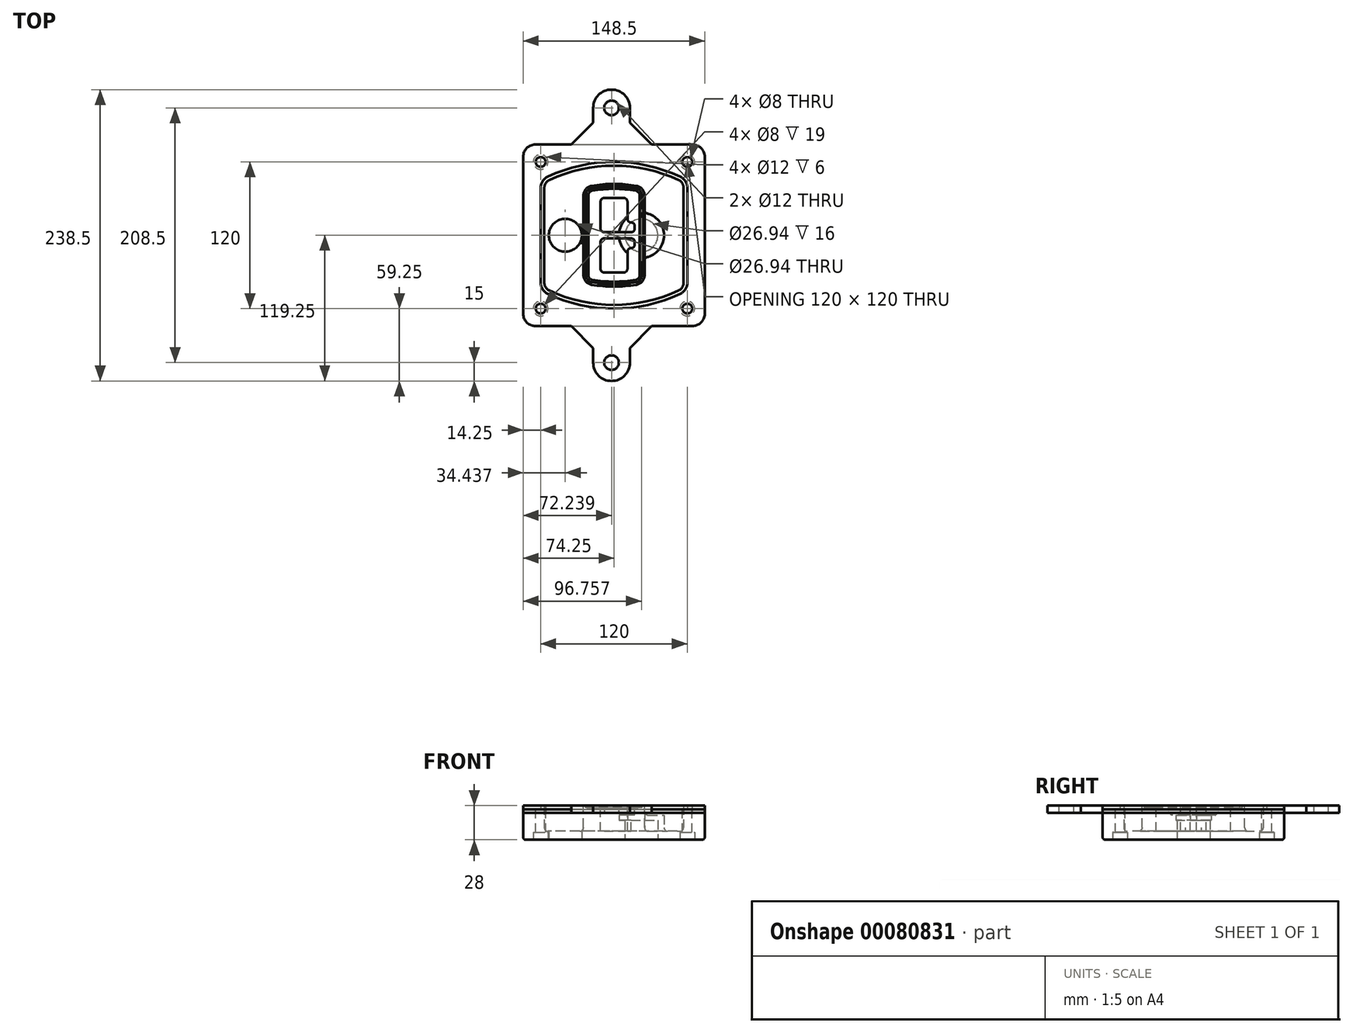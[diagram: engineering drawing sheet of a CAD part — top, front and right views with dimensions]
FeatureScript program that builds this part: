
annotation { "Feature Type Name" : "Feature", "Feature Type Description" : "" }
export const myFeature = defineFeature(function(context is Context, id is Id, definition is map)
    precondition{}
    {
        {
            var Q0;
            Q0=qCreatedBy(makeId("Top.planeOp"),FACE);
            var sketch = newSketch(context, id + "F0", { "sketchPlane" : qUnion([Q0])});
            skPoint(sketch, "E0.rect.middle", {"position": v(0, 0) * mm});
            skLineSegment(sketch, "E1.bottom", {"start": v(-64.25, -74.25) * mm, "end": v(64.25, -74.25) * mm});
            skLineSegment(sketch, "E1.top", {"start": v(-64.25, 74.25) * mm, "end": v(64.25, 74.25) * mm});
            skLineSegment(sketch, "E1.left", {"start": v(-74.25, -64.25) * mm, "end": v(-74.25, 64.25) * mm});
            skLineSegment(sketch, "E1.right", {"start": v(74.25, -64.25) * mm, "end": v(74.25, 64.25) * mm});
            skLineSegment(sketch, "E2", {"start": v(-74.25, 74.25) * mm, "end": v(74.25, -74.25) * mm, "construction": true});
            skLineSegment(sketch, "E3", {"start": v(74.25, 74.25) * mm, "end": v(-74.25, -74.25) * mm, "construction": true});
            skCircle(sketch, "E4", {"center": v(-60, 60) * mm, "radius": 4 * mm});
            skCircle(sketch, "E5", {"center": v(60, 60) * mm, "radius": 4 * mm});
            skCircle(sketch, "E6", {"center": v(60, -60) * mm, "radius": 4 * mm});
            skCircle(sketch, "E7", {"center": v(-60, -60) * mm, "radius": 4 * mm});
            skLineSegment(sketch, "E8", {"start": v(-60, 60) * mm, "end": v(60, 60) * mm, "construction": true});
            skLineSegment(sketch, "E9", {"start": v(60, 60) * mm, "end": v(60, -60) * mm, "construction": true});
            skLineSegment(sketch, "E10", {"start": v(60, -60) * mm, "end": v(-60, -60) * mm, "construction": true});
            skLineSegment(sketch, "E11", {"start": v(-60, -60) * mm, "end": v(-60, 60) * mm, "construction": true});
            skLineSegment(sketch, "E12", {"start": v(-60, 38.83) * mm, "end": v(-60, -38.83) * mm});
            skLineSegment(sketch, "E13", {"start": v(60, 38.83) * mm, "end": v(60, -38.83) * mm});
            skArc(sketch, "E14", {"start": v(54.26, 47.88) * mm, "mid": v(0, 60) * mm, "end": v(-54.26, 47.88) * mm});
            skArc(sketch, "E15", {"start": v(-54.26, -47.88) * mm, "mid": v(0, -60) * mm, "end": v(54.26, -47.88) * mm});
            skLineSegment(sketch, "E16", {"start": v(-60, 0) * mm, "end": v(60, 0) * mm, "construction": true});
            skPoint(sketch, "E17.visualSharp", {"position": v(-60, -45) * mm});
            skArc(sketch, "E17.filletArc", {"start": v(-60, -38.83) * mm, "mid": v(-58.44, -44.2) * mm, "end": v(-54.26, -47.88) * mm});
            skPoint(sketch, "E18.visualSharp", {"position": v(-60, 45) * mm});
            skArc(sketch, "E18.filletArc", {"start": v(-54.26, 47.88) * mm, "mid": v(-58.44, 44.2) * mm, "end": v(-60, 38.83) * mm});
            skPoint(sketch, "E19.visualSharp", {"position": v(60, 45) * mm});
            skArc(sketch, "E19.filletArc", {"start": v(60, 38.83) * mm, "mid": v(58.44, 44.2) * mm, "end": v(54.26, 47.88) * mm});
            skPoint(sketch, "E20.visualSharp", {"position": v(60, -45) * mm});
            skArc(sketch, "E20.filletArc", {"start": v(54.26, -47.88) * mm, "mid": v(58.44, -44.2) * mm, "end": v(60, -38.83) * mm});
            skPoint(sketch, "E21.visualSharp", {"position": v(-74.25, 74.25) * mm});
            skArc(sketch, "E21.filletArc", {"start": v(-64.25, 74.25) * mm, "mid": v(-71.32, 71.32) * mm, "end": v(-74.25, 64.25) * mm});
            skPoint(sketch, "E22.visualSharp", {"position": v(74.25, 74.25) * mm});
            skArc(sketch, "E22.filletArc", {"start": v(74.25, 64.25) * mm, "mid": v(71.32, 71.32) * mm, "end": v(64.25, 74.25) * mm});
            skPoint(sketch, "E23.visualSharp", {"position": v(74.25, -74.25) * mm});
            skArc(sketch, "E23.filletArc", {"start": v(64.25, -74.25) * mm, "mid": v(71.32, -71.32) * mm, "end": v(74.25, -64.25) * mm});
            skPoint(sketch, "E24.visualSharp", {"position": v(-74.25, -74.25) * mm});
            skArc(sketch, "E24.filletArc", {"start": v(-74.25, -64.25) * mm, "mid": v(-71.32, -71.32) * mm, "end": v(-64.25, -74.25) * mm});
            skArc(sketch, "E25.0", {"start": v(57, 38.83) * mm, "mid": v(55.9, 42.58) * mm, "end": v(52.98, 45.17) * mm});
            skLineSegment(sketch, "E25.1", {"start": v(57, 38.83) * mm, "end": v(57, -38.83) * mm});
            skArc(sketch, "E25.2", {"start": v(52.98, -45.17) * mm, "mid": v(55.9, -42.58) * mm, "end": v(57, -38.83) * mm});
            skArc(sketch, "E25.3", {"start": v(-52.98, -45.17) * mm, "mid": v(0, -57) * mm, "end": v(52.98, -45.17) * mm});
            skArc(sketch, "E25.4", {"start": v(-57, -38.83) * mm, "mid": v(-55.9, -42.58) * mm, "end": v(-52.98, -45.17) * mm});
            skArc(sketch, "E25.5", {"start": v(52.98, 45.17) * mm, "mid": v(0, 57) * mm, "end": v(-52.98, 45.17) * mm});
            skLineSegment(sketch, "E25.6", {"start": v(-57, 38.83) * mm, "end": v(-57, -38.83) * mm});
            skArc(sketch, "E25.7", {"start": v(-52.98, 45.17) * mm, "mid": v(-55.9, 42.58) * mm, "end": v(-57, 38.83) * mm});
            skArc(sketch, "E26.0", {"start": v(-55.96, 51.5) * mm, "mid": v(-61.82, 46.33) * mm, "end": v(-64, 38.83) * mm});
            skArc(sketch, "E26.1", {"start": v(55.96, 51.5) * mm, "mid": v(0, 64) * mm, "end": v(-55.96, 51.5) * mm});
            skArc(sketch, "E26.2", {"start": v(64, 38.83) * mm, "mid": v(61.82, 46.33) * mm, "end": v(55.96, 51.5) * mm});
            skLineSegment(sketch, "E26.3", {"start": v(64, 38.83) * mm, "end": v(64, -38.83) * mm});
            skArc(sketch, "E26.4", {"start": v(55.96, -51.5) * mm, "mid": v(61.82, -46.33) * mm, "end": v(64, -38.83) * mm});
            skLineSegment(sketch, "E26.5", {"start": v(-64, 38.83) * mm, "end": v(-64, -38.83) * mm});
            skArc(sketch, "E26.6", {"start": v(-55.96, -51.5) * mm, "mid": v(0, -64) * mm, "end": v(55.96, -51.5) * mm});
            skArc(sketch, "E26.7", {"start": v(-64, -38.83) * mm, "mid": v(-61.82, -46.33) * mm, "end": v(-55.96, -51.5) * mm});
            skSolve(sketch);
        }
        {
            var Q0;
            Q0=makeQuery(id+"F0.imprint","IMPRINT",FACE,{"disambiguationData":[TD([[makeQuery(id+"F0.imprint","IMPRINT",EDGE,{"derivedFrom":sQuery(id+"F0.wireOp",EDGE,"E1.bottom")}),1.0]])]});
            var Q1;
            Q1=makeQuery(id+"F0.imprint","IMPRINT",FACE,{"disambiguationData":[TD([[makeQuery(id+"F0.imprint","IMPRINT",EDGE,{"derivedFrom":sQuery(id+"F0.wireOp",EDGE,"E12")}),1.0]])]});
            var Q2;
            Q2=makeQuery(id+"F0.imprint","IMPRINT",FACE,{"disambiguationData":[TD([[makeQuery(id+"F0.imprint","IMPRINT",EDGE,{"derivedFrom":sQuery(id+"F0.wireOp",EDGE,"E25.0")}),1.0]])]});
            var Q3;
            Q3=makeQuery(id+"F0.imprint","IMPRINT",FACE,{"disambiguationData":[TD([[makeQuery(id+"F0.imprint","IMPRINT",EDGE,{"derivedFrom":sQuery(id+"F0.wireOp",EDGE,"E12")}),-1.0]])]});
            extrude(context, id + "F1", {"entities" : qUnion([Q0, Q1, Q2, Q3]), "oppositeDirection" : true, "depth" : 25 * mm});
        }
        {
            var Q0;
            Q0=makeQuery(id+"F0.imprint","IMPRINT",FACE,{"disambiguationData":[TD([[makeQuery(id+"F0.imprint","IMPRINT",EDGE,{"derivedFrom":sQuery(id+"F0.wireOp",EDGE,"E12")}),1.0]])]});
            extrude(context, id + "F2", {"entities" : qUnion([Q0]), "operationType" : NewBodyOperationType.ADD, "depth" : 3 * mm});
        }
        {
            var Q0;
            Q0=makeQuery(id+"F0.imprint","IMPRINT",FACE,{"disambiguationData":[TD([[makeQuery(id+"F0.imprint","IMPRINT",EDGE,{"derivedFrom":sQuery(id+"F0.wireOp",EDGE,"E25.0")}),1.0]])]});
            extrude(context, id + "F3", {"entities" : qUnion([Q0]), "operationType" : NewBodyOperationType.REMOVE, "oppositeDirection" : true, "depth" : 18 * mm});
        }
        {
            var Q0;
            Q0=makeQuery(id+"F2.opExtrude","CAP_FACE",FACE,{"disambiguationData":[OSD([sQuery(id+"F0.wireOp",EDGE,"E12"),sQuery(id+"F0.wireOp",EDGE,"E13"),sQuery(id+"F0.wireOp",EDGE,"E14"),sQuery(id+"F0.wireOp",EDGE,"E15"),sQuery(id+"F0.wireOp",EDGE,"E17.filletArc"),sQuery(id+"F0.wireOp",EDGE,"E18.filletArc"),sQuery(id+"F0.wireOp",EDGE,"E19.filletArc"),sQuery(id+"F0.wireOp",EDGE,"E20.filletArc"),sQuery(id+"F0.wireOp",EDGE,"E25.0"),sQuery(id+"F0.wireOp",EDGE,"E25.1"),sQuery(id+"F0.wireOp",EDGE,"E25.2"),sQuery(id+"F0.wireOp",EDGE,"E25.3"),sQuery(id+"F0.wireOp",EDGE,"E25.4"),sQuery(id+"F0.wireOp",EDGE,"E25.5"),sQuery(id+"F0.wireOp",EDGE,"E25.6"),sQuery(id+"F0.wireOp",EDGE,"E25.7")])],"isStart":false});
            var sketch = newSketch(context, id + "F4", { "sketchPlane" : qUnion([Q0])});
            skArc(sketch, "E27.0", {"start": v(-18.34, -40.45) * mm, "mid": v(0, -42) * mm, "end": v(18.34, -40.45) * mm});
            skArc(sketch, "E28.0", {"start": v(18.34, 40.45) * mm, "mid": v(0, 42) * mm, "end": v(-18.34, 40.45) * mm});
            skLineSegment(sketch, "E29", {"start": v(-25, 32.57) * mm, "end": v(-25, -32.57) * mm});
            skLineSegment(sketch, "E30", {"start": v(25, 32.57) * mm, "end": v(25, -32.57) * mm});
            skLineSegment(sketch, "E31", {"start": v(-25, 39.1) * mm, "end": v(25, 39.1) * mm, "construction": true});
            skLineSegment(sketch, "E32", {"start": v(-25, -39.1) * mm, "end": v(25, -39.1) * mm, "construction": true});
            skPoint(sketch, "E33.visualSharp", {"position": v(-25, 39.1) * mm});
            skArc(sketch, "E33.filletArc", {"start": v(-18.34, 40.45) * mm, "mid": v(-23.11, 37.73) * mm, "end": v(-25, 32.57) * mm});
            skPoint(sketch, "E34.visualSharp", {"position": v(25, 39.1) * mm});
            skArc(sketch, "E34.filletArc", {"start": v(25, 32.57) * mm, "mid": v(23.11, 37.73) * mm, "end": v(18.34, 40.45) * mm});
            skPoint(sketch, "E35.visualSharp", {"position": v(25, -39.1) * mm});
            skArc(sketch, "E35.filletArc", {"start": v(18.34, -40.45) * mm, "mid": v(23.11, -37.73) * mm, "end": v(25, -32.57) * mm});
            skPoint(sketch, "E36.visualSharp", {"position": v(-25, -39.1) * mm});
            skArc(sketch, "E36.filletArc", {"start": v(-25, -32.57) * mm, "mid": v(-23.11, -37.73) * mm, "end": v(-18.34, -40.45) * mm});
            skArc(sketch, "E37.0", {"start": v(52.98, 45.17) * mm, "mid": v(0, 57) * mm, "end": v(-52.98, 45.17) * mm});
            skArc(sketch, "E37.1", {"start": v(-52.98, 45.17) * mm, "mid": v(-55.9, 42.58) * mm, "end": v(-57, 38.83) * mm});
            skLineSegment(sketch, "E37.2", {"start": v(-57, 38.83) * mm, "end": v(-57, -38.83) * mm});
            skArc(sketch, "E37.3", {"start": v(-57, -38.83) * mm, "mid": v(-55.9, -42.58) * mm, "end": v(-52.98, -45.17) * mm});
            skArc(sketch, "E37.4", {"start": v(-52.98, -45.17) * mm, "mid": v(0, -57) * mm, "end": v(52.98, -45.17) * mm});
            skArc(sketch, "E37.5", {"start": v(52.98, -45.17) * mm, "mid": v(55.9, -42.58) * mm, "end": v(57, -38.83) * mm});
            skLineSegment(sketch, "E37.6", {"start": v(57, 38.83) * mm, "end": v(57, -38.83) * mm});
            skArc(sketch, "E37.7", {"start": v(57, 38.83) * mm, "mid": v(55.9, 42.58) * mm, "end": v(52.98, 45.17) * mm});
            skLineSegment(sketch, "E38.0", {"start": v(23, 32.57) * mm, "end": v(23, -32.57) * mm});
            skArc(sketch, "E38.1", {"start": v(18, -38.48) * mm, "mid": v(21.58, -36.44) * mm, "end": v(23, -32.57) * mm});
            skArc(sketch, "E38.2", {"start": v(-18, -38.48) * mm, "mid": v(0, -40) * mm, "end": v(18, -38.48) * mm});
            skArc(sketch, "E38.3", {"start": v(-23, -32.57) * mm, "mid": v(-21.58, -36.44) * mm, "end": v(-18, -38.48) * mm});
            skLineSegment(sketch, "E38.4", {"start": v(-23, 32.57) * mm, "end": v(-23, -32.57) * mm});
            skArc(sketch, "E38.5", {"start": v(23, 32.57) * mm, "mid": v(21.58, 36.44) * mm, "end": v(18, 38.48) * mm});
            skArc(sketch, "E38.6", {"start": v(-18, 38.48) * mm, "mid": v(-21.58, 36.44) * mm, "end": v(-23, 32.57) * mm});
            skArc(sketch, "E38.7", {"start": v(18, 38.48) * mm, "mid": v(0, 40) * mm, "end": v(-18, 38.48) * mm});
            skArc(sketch, "E39.0", {"start": v(21, 32.57) * mm, "mid": v(20.06, 35.15) * mm, "end": v(17.67, 36.5) * mm});
            skLineSegment(sketch, "E39.1", {"start": v(21, 32.57) * mm, "end": v(21, -32.57) * mm});
            skArc(sketch, "E39.2", {"start": v(17.67, -36.5) * mm, "mid": v(20.06, -35.15) * mm, "end": v(21, -32.57) * mm});
            skArc(sketch, "E39.3", {"start": v(-17.67, -36.5) * mm, "mid": v(0, -38) * mm, "end": v(17.67, -36.5) * mm});
            skArc(sketch, "E39.4", {"start": v(-21, -32.57) * mm, "mid": v(-20.06, -35.15) * mm, "end": v(-17.67, -36.5) * mm});
            skArc(sketch, "E39.5", {"start": v(17.67, 36.5) * mm, "mid": v(0, 38) * mm, "end": v(-17.67, 36.5) * mm});
            skLineSegment(sketch, "E39.6", {"start": v(-21, 32.57) * mm, "end": v(-21, -32.57) * mm});
            skArc(sketch, "E39.7", {"start": v(-17.67, 36.5) * mm, "mid": v(-20.06, 35.15) * mm, "end": v(-21, 32.57) * mm});
            skLineSegment(sketch, "E40", {"start": v(-25, 0) * mm, "end": v(25, 0) * mm, "construction": true});
            skLineSegment(sketch, "E41", {"start": v(-11, 5.5) * mm, "end": v(-11, 27.5) * mm});
            skLineSegment(sketch, "E42", {"start": v(-8, 30.5) * mm, "end": v(8, 30.5) * mm});
            skLineSegment(sketch, "E43", {"start": v(11, 27.5) * mm, "end": v(11, 13.5) * mm});
            skLineSegment(sketch, "E44", {"start": v(14, 10.5) * mm, "end": v(14, 10.5) * mm});
            skLineSegment(sketch, "E45", {"start": v(17, 7.5) * mm, "end": v(17, 5.5) * mm});
            skLineSegment(sketch, "E46", {"start": v(14, 2.5) * mm, "end": v(-8, 2.5) * mm});
            skPoint(sketch, "E47.visualSharp", {"position": v(-11, 30.5) * mm});
            skArc(sketch, "E47.filletArc", {"start": v(-8, 30.5) * mm, "mid": v(-10.12, 29.62) * mm, "end": v(-11, 27.5) * mm});
            skPoint(sketch, "E48.visualSharp", {"position": v(11, 30.5) * mm});
            skArc(sketch, "E48.filletArc", {"start": v(11, 27.5) * mm, "mid": v(10.12, 29.62) * mm, "end": v(8, 30.5) * mm});
            skPoint(sketch, "E49.visualSharp", {"position": v(11, 10.5) * mm});
            skArc(sketch, "E49.filletArc", {"start": v(11, 13.5) * mm, "mid": v(11.88, 11.38) * mm, "end": v(14, 10.5) * mm});
            skPoint(sketch, "E50.visualSharp", {"position": v(17, 10.5) * mm});
            skArc(sketch, "E50.filletArc", {"start": v(17, 7.5) * mm, "mid": v(16.12, 9.62) * mm, "end": v(14, 10.5) * mm});
            skPoint(sketch, "E51.visualSharp", {"position": v(17, 2.5) * mm});
            skArc(sketch, "E51.filletArc", {"start": v(14, 2.5) * mm, "mid": v(16.12, 3.38) * mm, "end": v(17, 5.5) * mm});
            skPoint(sketch, "E52.visualSharp", {"position": v(-11, 2.5) * mm});
            skArc(sketch, "E52.filletArc", {"start": v(-11, 5.5) * mm, "mid": v(-10.12, 3.38) * mm, "end": v(-8, 2.5) * mm});
            skLineSegment(sketch, "E53.0.MirrorCS", {"start": v(14, -2.5) * mm, "end": v(-8, -2.5) * mm});
            skArc(sketch, "E54.0.MirrorCS", {"start": v(-11, -5.5) * mm, "mid": v(-10.12, -3.38) * mm, "end": v(-8, -2.5) * mm});
            skLineSegment(sketch, "E55.0.MirrorCS", {"start": v(-11, -5.5) * mm, "end": v(-11, -27.5) * mm});
            skArc(sketch, "E56.0.MirrorCS", {"start": v(-8, -30.5) * mm, "mid": v(-10.12, -29.62) * mm, "end": v(-11, -27.5) * mm});
            skLineSegment(sketch, "E57.0.MirrorCS", {"start": v(-8, -30.5) * mm, "end": v(8, -30.5) * mm});
            skArc(sketch, "E58.0.MirrorCS", {"start": v(11, -27.5) * mm, "mid": v(10.12, -29.62) * mm, "end": v(8, -30.5) * mm});
            skLineSegment(sketch, "E59.0.MirrorCS", {"start": v(11, -27.5) * mm, "end": v(11, -13.5) * mm});
            skArc(sketch, "E60.0.MirrorCS", {"start": v(11, -13.5) * mm, "mid": v(11.88, -11.38) * mm, "end": v(14, -10.5) * mm});
            skArc(sketch, "E61.0.MirrorCS", {"start": v(17, -7.5) * mm, "mid": v(16.12, -9.62) * mm, "end": v(14, -10.5) * mm});
            skLineSegment(sketch, "E62.0.MirrorCS", {"start": v(17, -7.5) * mm, "end": v(17, -5.5) * mm});
            skArc(sketch, "E63.0.MirrorCS", {"start": v(14, -2.5) * mm, "mid": v(16.12, -3.38) * mm, "end": v(17, -5.5) * mm});
            skSolve(sketch);
        }
        {
            var Q0;
            Q0=makeQuery(id+"F4.imprint","IMPRINT",FACE,{"disambiguationData":[TD([[makeQuery(id+"F4.imprint","IMPRINT",EDGE,{"derivedFrom":sQuery(id+"F4.wireOp",EDGE,"E27.0")}),1.0]])]});
            var Q1;
            Q1=makeQuery(id+"F4.imprint","IMPRINT",FACE,{"disambiguationData":[TD([[makeQuery(id+"F4.imprint","IMPRINT",EDGE,{"derivedFrom":sQuery(id+"F4.wireOp",EDGE,"E38.0")}),-1.0]])]});
            var Q2;
            Q2=makeQuery(id+"F4.imprint","IMPRINT",FACE,{"disambiguationData":[TD([[makeQuery(id+"F4.imprint","IMPRINT",EDGE,{"derivedFrom":sQuery(id+"F4.wireOp",EDGE,"E39.0")}),1.0]])]});
            extrude(context, id + "F5", {"entities" : qUnion([Q0, Q1, Q2]), "operationType" : NewBodyOperationType.ADD, "endBound" : BoundingType.UP_TO_NEXT, "oppositeDirection" : true, "depth" : 25 * mm});
        }
        {
            var Q0;
            Q0=makeQuery(id+"F4.imprint","IMPRINT",FACE,{"disambiguationData":[TD([[makeQuery(id+"F4.imprint","IMPRINT",EDGE,{"derivedFrom":sQuery(id+"F4.wireOp",EDGE,"E38.0")}),-1.0]])]});
            extrude(context, id + "F6", {"entities" : qUnion([Q0]), "operationType" : NewBodyOperationType.REMOVE, "oppositeDirection" : true, "depth" : 2 * mm});
        }
        {
            var Q0;
            Q0=makeQuery(id+"F1.opExtrude","CAP_FACE",FACE,{"disambiguationData":[OSD([sQuery(id+"F0.wireOp",EDGE,"E1.bottom"),sQuery(id+"F0.wireOp",EDGE,"E1.top"),sQuery(id+"F0.wireOp",EDGE,"E1.left"),sQuery(id+"F0.wireOp",EDGE,"E1.right"),sQuery(id+"F0.wireOp",EDGE,"E4"),sQuery(id+"F0.wireOp",EDGE,"E5"),sQuery(id+"F0.wireOp",EDGE,"E6"),sQuery(id+"F0.wireOp",EDGE,"E7"),sQuery(id+"F0.wireOp",EDGE,"E21.filletArc"),sQuery(id+"F0.wireOp",EDGE,"E22.filletArc"),sQuery(id+"F0.wireOp",EDGE,"E23.filletArc"),sQuery(id+"F0.wireOp",EDGE,"E24.filletArc")])],"isStart":false});
            var sketch = newSketch(context, id + "F7", { "sketchPlane" : qUnion([Q0])});
            skCircle(sketch, "E64", {"center": v(22.5, 0) * mm, "radius": 13.47 * mm});
            skCircle(sketch, "E65", {"center": v(-39.81, 0) * mm, "radius": 13.47 * mm});
            skLineSegment(sketch, "E66", {"start": v(74.25, 0) * mm, "end": v(-74.25, 0) * mm});
            skCircle(sketch, "E67", {"center": v(22.5, 0) * mm, "radius": 18.47 * mm});
            skCircle(sketch, "E68", {"center": v(60, -60) * mm, "radius": 6 * mm});
            skCircle(sketch, "E69", {"center": v(-60, -60) * mm, "radius": 6 * mm});
            skCircle(sketch, "E70", {"center": v(-60, 60) * mm, "radius": 6 * mm});
            skCircle(sketch, "E71", {"center": v(60, 60) * mm, "radius": 6 * mm});
            skSolve(sketch);
        }
        {
            var Q0;
            {var subQ1=sQuery(id+"F7.wireOp",EDGE,"E66");var subQ4=sQuery(id+"F7.wireOp",EDGE,"E64");var subQ6=makeQuery(id+"F7.imprint","INTERSECT",VERTEX,{"disambiguationData":[OD(0.0)],"derivedFrom":[subQ4,subQ1]});Q0=makeQuery(id+"F7.imprint","IMPRINT",FACE,{"disambiguationData":[TD([[makeQuery(id+"F7.imprint","IMPRINT",EDGE,{"disambiguationData":[TD([[subQ6,-1.0]])],"derivedFrom":subQ4}),-1.0]])]});}
            var Q1;
            {var subQ0=sQuery(id+"F7.wireOp",EDGE,"E66");var subQ1=sQuery(id+"F7.wireOp",EDGE,"E64");var subQ3=makeQuery(id+"F7.imprint","INTERSECT",VERTEX,{"disambiguationData":[OD(0.0)],"derivedFrom":[subQ1,subQ0]});Q1=makeQuery(id+"F7.imprint","IMPRINT",FACE,{"disambiguationData":[TD([[makeQuery(id+"F7.imprint","IMPRINT",EDGE,{"disambiguationData":[TD([[subQ3,-1.0]])],"derivedFrom":subQ1}),1.0]])]});}
            var Q2;
            {var subQ0=sQuery(id+"F7.wireOp",EDGE,"E66");var subQ1=sQuery(id+"F7.wireOp",EDGE,"E64");var subQ3=makeQuery(id+"F7.imprint","INTERSECT",VERTEX,{"disambiguationData":[OD(0.0)],"derivedFrom":[subQ1,subQ0]});Q2=makeQuery(id+"F7.imprint","IMPRINT",FACE,{"disambiguationData":[TD([[makeQuery(id+"F7.imprint","IMPRINT",EDGE,{"disambiguationData":[TD([[subQ3,1.0]])],"derivedFrom":subQ1}),1.0]])]});}
            var Q3;
            {var subQ1=sQuery(id+"F7.wireOp",EDGE,"E66");var subQ4=sQuery(id+"F7.wireOp",EDGE,"E64");var subQ6=makeQuery(id+"F7.imprint","INTERSECT",VERTEX,{"disambiguationData":[OD(0.0)],"derivedFrom":[subQ4,subQ1]});Q3=makeQuery(id+"F7.imprint","IMPRINT",FACE,{"disambiguationData":[TD([[makeQuery(id+"F7.imprint","IMPRINT",EDGE,{"disambiguationData":[TD([[subQ6,1.0]])],"derivedFrom":subQ4}),-1.0]])]});}
            extrude(context, id + "F8", {"entities" : qUnion([Q0, Q1, Q2, Q3]), "operationType" : NewBodyOperationType.ADD, "oppositeDirection" : true, "depth" : 20 * mm});
        }
        {
            var Q0;
            {var subQ0=sQuery(id+"F7.wireOp",EDGE,"E66");var subQ1=sQuery(id+"F7.wireOp",EDGE,"E64");var subQ3=makeQuery(id+"F7.imprint","INTERSECT",VERTEX,{"disambiguationData":[OD(0.0)],"derivedFrom":[subQ1,subQ0]});Q0=makeQuery(id+"F7.imprint","IMPRINT",FACE,{"disambiguationData":[TD([[makeQuery(id+"F7.imprint","IMPRINT",EDGE,{"disambiguationData":[TD([[subQ3,-1.0]])],"derivedFrom":subQ1}),1.0]])]});}
            var Q1;
            {var subQ0=sQuery(id+"F7.wireOp",EDGE,"E66");var subQ1=sQuery(id+"F7.wireOp",EDGE,"E64");var subQ3=makeQuery(id+"F7.imprint","INTERSECT",VERTEX,{"disambiguationData":[OD(0.0)],"derivedFrom":[subQ1,subQ0]});Q1=makeQuery(id+"F7.imprint","IMPRINT",FACE,{"disambiguationData":[TD([[makeQuery(id+"F7.imprint","IMPRINT",EDGE,{"disambiguationData":[TD([[subQ3,1.0]])],"derivedFrom":subQ1}),1.0]])]});}
            extrude(context, id + "F9", {"entities" : qUnion([Q0, Q1]), "operationType" : NewBodyOperationType.REMOVE, "oppositeDirection" : true, "depth" : 16 * mm});
        }
        {
            var Q0;
            {var subQ0=sQuery(id+"F7.wireOp",EDGE,"E66");var subQ1=sQuery(id+"F7.wireOp",EDGE,"E65");var subQ3=makeQuery(id+"F7.imprint","INTERSECT",VERTEX,{"disambiguationData":[OD(0.0)],"derivedFrom":[subQ1,subQ0]});Q0=makeQuery(id+"F7.imprint","IMPRINT",FACE,{"disambiguationData":[TD([[makeQuery(id+"F7.imprint","IMPRINT",EDGE,{"disambiguationData":[TD([[subQ3,-1.0]])],"derivedFrom":subQ1}),1.0]])]});}
            var Q1;
            {var subQ0=sQuery(id+"F7.wireOp",EDGE,"E66");var subQ1=sQuery(id+"F7.wireOp",EDGE,"E65");var subQ3=makeQuery(id+"F7.imprint","INTERSECT",VERTEX,{"disambiguationData":[OD(0.0)],"derivedFrom":[subQ1,subQ0]});Q1=makeQuery(id+"F7.imprint","IMPRINT",FACE,{"disambiguationData":[TD([[makeQuery(id+"F7.imprint","IMPRINT",EDGE,{"disambiguationData":[TD([[subQ3,1.0]])],"derivedFrom":subQ1}),1.0]])]});}
            extrude(context, id + "F10", {"entities" : qUnion([Q0, Q1]), "operationType" : NewBodyOperationType.REMOVE, "oppositeDirection" : true, "depth" : 25 * mm});
        }
        {
            var Q0;
            Q0=makeQuery(id+"F7.imprint","IMPRINT",FACE,{"disambiguationData":[TD([[makeQuery(id+"F7.imprint","IMPRINT",EDGE,{"derivedFrom":sQuery(id+"F7.wireOp",EDGE,"E68")}),1.0]])]});
            var Q1;
            Q1=makeQuery(id+"F7.imprint","IMPRINT",FACE,{"disambiguationData":[TD([[makeQuery(id+"F7.imprint","IMPRINT",EDGE,{"derivedFrom":makeQuery(id+"F1.opExtrude","CAP_EDGE",EDGE,{"disambiguationData":[OSD([sQuery(id+"F0.wireOp",EDGE,"E5")])],"isStart":false})}),-1.0]])]});
            var Q2;
            Q2=makeQuery(id+"F7.imprint","IMPRINT",FACE,{"disambiguationData":[TD([[makeQuery(id+"F7.imprint","IMPRINT",EDGE,{"derivedFrom":sQuery(id+"F7.wireOp",EDGE,"E69")}),1.0]])]});
            var Q3;
            Q3=makeQuery(id+"F7.imprint","IMPRINT",FACE,{"disambiguationData":[TD([[makeQuery(id+"F7.imprint","IMPRINT",EDGE,{"derivedFrom":makeQuery(id+"F1.opExtrude","CAP_EDGE",EDGE,{"disambiguationData":[OSD([sQuery(id+"F0.wireOp",EDGE,"E4")])],"isStart":false})}),-1.0]])]});
            var Q4;
            Q4=makeQuery(id+"F7.imprint","IMPRINT",FACE,{"disambiguationData":[TD([[makeQuery(id+"F7.imprint","IMPRINT",EDGE,{"derivedFrom":sQuery(id+"F7.wireOp",EDGE,"E70")}),1.0]])]});
            var Q5;
            Q5=makeQuery(id+"F7.imprint","IMPRINT",FACE,{"disambiguationData":[TD([[makeQuery(id+"F7.imprint","IMPRINT",EDGE,{"derivedFrom":makeQuery(id+"F1.opExtrude","CAP_EDGE",EDGE,{"disambiguationData":[OSD([sQuery(id+"F0.wireOp",EDGE,"E7")])],"isStart":false})}),-1.0]])]});
            var Q6;
            Q6=makeQuery(id+"F7.imprint","IMPRINT",FACE,{"disambiguationData":[TD([[makeQuery(id+"F7.imprint","IMPRINT",EDGE,{"derivedFrom":sQuery(id+"F7.wireOp",EDGE,"E71")}),1.0]])]});
            var Q7;
            Q7=makeQuery(id+"F7.imprint","IMPRINT",FACE,{"disambiguationData":[TD([[makeQuery(id+"F7.imprint","IMPRINT",EDGE,{"derivedFrom":makeQuery(id+"F1.opExtrude","CAP_EDGE",EDGE,{"disambiguationData":[OSD([sQuery(id+"F0.wireOp",EDGE,"E6")])],"isStart":false})}),-1.0]])]});
            extrude(context, id + "F11", {"entities" : qUnion([Q0, Q1, Q2, Q3, Q4, Q5, Q6, Q7]), "operationType" : NewBodyOperationType.REMOVE, "oppositeDirection" : true, "depth" : 6 * mm});
        }
        {
            var Q0;
            Q0=makeQuery(id+"F9.boolean.opBoolean","COPY",FACE,{"derivedFrom":makeQuery(id+"F9.opExtrude","CAP_FACE",FACE,{"disambiguationData":[OSD([sQuery(id+"F7.wireOp",EDGE,"E64")])],"isStart":false})});
            var sketch = newSketch(context, id + "F12", { "sketchPlane" : qUnion([Q0])});
            skArc(sketch, "E72.0", {"start": v(11, 14.45) * mm, "mid": v(6.45, 9.13) * mm, "end": v(4.2, 2.5) * mm});
            skArc(sketch, "E72.1", {"start": v(4.2, -2.5) * mm, "mid": v(6.45, -9.13) * mm, "end": v(11, -14.45) * mm});
            skLineSegment(sketch, "E73", {"start": v(4.2, -2.5) * mm, "end": v(14, -2.5) * mm});
            skLineSegment(sketch, "E74.0", {"start": v(14, 2.5) * mm, "end": v(4.2, 2.5) * mm});
            skArc(sketch, "E74.1", {"start": v(14, 2.5) * mm, "mid": v(16.12, 3.38) * mm, "end": v(17, 5.5) * mm});
            skLineSegment(sketch, "E74.2", {"start": v(17, 7.5) * mm, "end": v(17, 5.5) * mm});
            skArc(sketch, "E74.3", {"start": v(17, 7.5) * mm, "mid": v(16.12, 9.62) * mm, "end": v(14, 10.5) * mm});
            skArc(sketch, "E74.4", {"start": v(11, 13.5) * mm, "mid": v(11.88, 11.38) * mm, "end": v(14, 10.5) * mm});
            skLineSegment(sketch, "E74.5", {"start": v(11, 14.45) * mm, "end": v(11, 13.5) * mm});
            skLineSegment(sketch, "E74.7", {"start": v(14, -2.5) * mm, "end": v(4.2, -2.5) * mm});
            skArc(sketch, "E74.8", {"start": v(14, -2.5) * mm, "mid": v(16.12, -3.38) * mm, "end": v(17, -5.5) * mm});
            skLineSegment(sketch, "E74.9", {"start": v(17, -7.5) * mm, "end": v(17, -5.5) * mm});
            skArc(sketch, "E74.10", {"start": v(17, -7.5) * mm, "mid": v(16.12, -9.62) * mm, "end": v(14, -10.5) * mm});
            skArc(sketch, "E74.11", {"start": v(11, -13.5) * mm, "mid": v(11.88, -11.38) * mm, "end": v(14, -10.5) * mm});
            skLineSegment(sketch, "E74.12", {"start": v(11, -14.45) * mm, "end": v(11, -13.5) * mm});
            skPoint(sketch, "E75.orphan", {"position": v(11, -27.5) * mm});
            skPoint(sketch, "E76.orphan", {"position": v(-8, -2.5) * mm});
            skPoint(sketch, "E77.orphan", {"position": v(-8, 2.5) * mm});
            skPoint(sketch, "E78.orphan", {"position": v(11, 27.5) * mm});
            skSolve(sketch);
        }
        {
            var Q0;
            {var subQ7=sQuery(id+"F12.wireOp",EDGE,"E72.0");var subQ14=sQuery(id+"F12.wireOp",EDGE,"E72.1");var subQ16=sQuery(id+"F12.wireOp",EDGE,"E74.1");var subQ18=sQuery(id+"F12.wireOp",EDGE,"E74.8");Q0=qUnion([makeQuery(id+"F12.imprint","IMPRINT",FACE,{"disambiguationData":[TD([[makeQuery(id+"F12.imprint","IMPRINT",EDGE,{"derivedFrom":subQ7}),1.0]])]}),makeQuery(id+"F12.imprint","IMPRINT",FACE,{"disambiguationData":[TD([[makeQuery(id+"F12.imprint","IMPRINT",EDGE,{"derivedFrom":subQ14}),1.0]])]}),makeQuery(id+"F12.imprint","IMPRINT",FACE,{"disambiguationData":[TD([[makeQuery(id+"F12.imprint","IMPRINT",EDGE,{"derivedFrom":subQ16}),1.0]])]}),makeQuery(id+"F12.imprint","IMPRINT",FACE,{"disambiguationData":[TD([[makeQuery(id+"F12.imprint","IMPRINT",EDGE,{"derivedFrom":subQ18}),-1.0]])]})]);}
            var Q1;
            Q1=makeQuery(id+"F5.boolean.opBoolean","SPLIT",FACE,{"disambiguationData":[TD([makeQuery(id+"F5.opExtrude","SWEPT_FACE",FACE,{"disambiguationData":[OSD([sQuery(id+"F4.wireOp",EDGE,"E41")])]})])],"derivedFrom":makeQuery(id+"F3.boolean.opBoolean","COPY",FACE,{"derivedFrom":makeQuery(id+"F3.opExtrude","CAP_FACE",FACE,{"disambiguationData":[OSD([sQuery(id+"F0.wireOp",EDGE,"E25.0"),sQuery(id+"F0.wireOp",EDGE,"E25.1"),sQuery(id+"F0.wireOp",EDGE,"E25.2"),sQuery(id+"F0.wireOp",EDGE,"E25.3"),sQuery(id+"F0.wireOp",EDGE,"E25.4"),sQuery(id+"F0.wireOp",EDGE,"E25.5"),sQuery(id+"F0.wireOp",EDGE,"E25.6"),sQuery(id+"F0.wireOp",EDGE,"E25.7")])],"isStart":false})})});
            extrude(context, id + "F13", {"entities" : qUnion([Q0]), "operationType" : NewBodyOperationType.REMOVE, "endBound" : BoundingType.UP_TO_SURFACE, "endBoundEntityFace" : qUnion([Q1]), "depth" : 25 * mm});
        }
        {
            var Q0;
            Q0=makeQuery(id+"F3.boolean.opBoolean","COPY",EDGE,{"derivedFrom":makeQuery(id+"F3.opExtrude","CAP_EDGE",EDGE,{"disambiguationData":[OSD([sQuery(id+"F0.wireOp",EDGE,"E25.6")])],"isStart":false})});
            var Q1;
            Q1=makeQuery(id+"F8.boolean.opBoolean","INTERSECT",EDGE,{"derivedFrom":[makeQuery(id+"F5.opExtrude","SWEPT_FACE",FACE,{"disambiguationData":[OSD([sQuery(id+"F4.wireOp",EDGE,"E30")])]}),makeQuery(id+"F8.opExtrude","CAP_FACE",FACE,{"disambiguationData":[OSD([sQuery(id+"F7.wireOp",EDGE,"E67")])],"isStart":false})]});
            var Q2;
            Q2=makeQuery(id+"F8.boolean.opBoolean","INTERSECT",EDGE,{"disambiguationData":[OD(1.0)],"derivedFrom":[makeQuery(id+"F5.opExtrude","SWEPT_FACE",FACE,{"disambiguationData":[OSD([sQuery(id+"F4.wireOp",EDGE,"E30")])]}),makeQuery(id+"F8.opExtrude","SWEPT_FACE",FACE,{"disambiguationData":[OSD([sQuery(id+"F7.wireOp",EDGE,"E67")])]})]});
            var Q3;
            {var subQ0=sQuery(id+"F4.wireOp",EDGE,"E30");Q3=makeQuery(id+"F8.boolean.opBoolean","SPLIT",EDGE,{"disambiguationData":[TD([makeQuery(id+"F5.opExtrude","SWEPT_FACE",FACE,{"disambiguationData":[OSD([sQuery(id+"F4.wireOp",EDGE,"E35.filletArc")])]})])],"derivedFrom":makeQuery(id+"F5.opExtrude","CAP_EDGE",EDGE,{"disambiguationData":[OSD([subQ0])],"isStart":false})});}
            var Q4;
            {var subQ0=sQuery(id+"F0.wireOp",EDGE,"E25.7");var subQ1=sQuery(id+"F0.wireOp",EDGE,"E25.1");var subQ2=sQuery(id+"F0.wireOp",EDGE,"E25.6");var subQ3=sQuery(id+"F0.wireOp",EDGE,"E25.5");var subQ4=sQuery(id+"F0.wireOp",EDGE,"E25.4");var subQ5=sQuery(id+"F0.wireOp",EDGE,"E25.0");var subQ6=sQuery(id+"F0.wireOp",EDGE,"E25.2");var subQ7=sQuery(id+"F0.wireOp",EDGE,"E25.3");Q4=makeQuery(id+"F8.boolean.opBoolean","INTERSECT",EDGE,{"derivedFrom":[makeQuery(id+"F5.boolean.opBoolean","SPLIT",FACE,{"disambiguationData":[TD([makeQuery(id+"F2.opExtrude","SWEPT_FACE",FACE,{"disambiguationData":[OSD([subQ5])]})])],"derivedFrom":makeQuery(id+"F3.boolean.opBoolean","COPY",FACE,{"derivedFrom":makeQuery(id+"F3.opExtrude","CAP_FACE",FACE,{"disambiguationData":[OSD([subQ5,subQ1,subQ6,subQ7,subQ4,subQ3,subQ2,subQ0])],"isStart":false})})}),makeQuery(id+"F8.opExtrude","SWEPT_FACE",FACE,{"disambiguationData":[OSD([sQuery(id+"F7.wireOp",EDGE,"E67")])]})]});}
            var Q5;
            Q5=makeQuery(id+"F8.boolean.opBoolean","INTERSECT",EDGE,{"disambiguationData":[OD(0.0)],"derivedFrom":[makeQuery(id+"F5.opExtrude","SWEPT_FACE",FACE,{"disambiguationData":[OSD([sQuery(id+"F4.wireOp",EDGE,"E30")])]}),makeQuery(id+"F8.opExtrude","SWEPT_FACE",FACE,{"disambiguationData":[OSD([sQuery(id+"F7.wireOp",EDGE,"E67")])]})]});
            fillet(context, id + "F14", {"entities" : qUnion([Q0, Q1, Q2, Q3, Q4, Q5]), "radius" : 3 * mm, "tangentPropagation" : true, "allowEdgeOverflow" : false});
        }
        {
            var Q0;
            Q0=makeQuery(id+"F1.opExtrude","CAP_EDGE",EDGE,{"disambiguationData":[OSD([sQuery(id+"F0.wireOp",EDGE,"E1.bottom")])],"isStart":false});
            fillet(context, id + "F15", {"entities" : qUnion([Q0]), "radius" : 2 * mm, "tangentPropagation" : true, "allowEdgeOverflow" : false});
        }
        {
            var Q0;
            Q0=qCreatedBy(makeId("Top.planeOp"),FACE);
            var sketch = newSketch(context, id + "F16", { "sketchPlane" : qUnion([Q0])});
            skArc(sketch, "E79.0", {"start": v(54.26, 47.88) * mm, "mid": v(0, 60) * mm, "end": v(-54.26, 47.88) * mm});
            skArc(sketch, "E79.1", {"start": v(60, 38.83) * mm, "mid": v(58.44, 44.2) * mm, "end": v(54.26, 47.88) * mm});
            skArc(sketch, "E79.2", {"start": v(-54.26, 47.88) * mm, "mid": v(-58.44, 44.2) * mm, "end": v(-60, 38.83) * mm});
            skLineSegment(sketch, "E79.3", {"start": v(-60, 38.83) * mm, "end": v(-60, -38.83) * mm});
            skArc(sketch, "E79.4", {"start": v(-60, -38.83) * mm, "mid": v(-58.44, -44.2) * mm, "end": v(-54.26, -47.88) * mm});
            skArc(sketch, "E79.5", {"start": v(-54.26, -47.88) * mm, "mid": v(0, -60) * mm, "end": v(54.26, -47.88) * mm});
            skArc(sketch, "E79.6", {"start": v(54.26, -47.88) * mm, "mid": v(58.44, -44.2) * mm, "end": v(60, -38.83) * mm});
            skLineSegment(sketch, "E79.7", {"start": v(60, 38.83) * mm, "end": v(60, -38.83) * mm});
            skCircle(sketch, "E79.8", {"center": v(60, 60) * mm, "radius": 4 * mm});
            skCircle(sketch, "E79.9", {"center": v(-60, 60) * mm, "radius": 4 * mm});
            skCircle(sketch, "E79.10", {"center": v(-60, -60) * mm, "radius": 4 * mm});
            skCircle(sketch, "E79.11", {"center": v(60, -60) * mm, "radius": 4 * mm});
            skLineSegment(sketch, "E79.12", {"start": v(-64.25, 74.25) * mm, "end": v(64.25, 74.25) * mm});
            skArc(sketch, "E79.13", {"start": v(-64.25, 74.25) * mm, "mid": v(-71.32, 71.32) * mm, "end": v(-74.25, 64.25) * mm});
            skLineSegment(sketch, "E79.14", {"start": v(-74.25, -64.25) * mm, "end": v(-74.25, 64.25) * mm});
            skLineSegment(sketch, "E79.15", {"start": v(74.25, -64.25) * mm, "end": v(74.25, 64.25) * mm});
            skArc(sketch, "E79.16", {"start": v(74.25, 64.25) * mm, "mid": v(71.32, 71.32) * mm, "end": v(64.25, 74.25) * mm});
            skArc(sketch, "E79.17", {"start": v(64.25, -74.25) * mm, "mid": v(71.32, -71.32) * mm, "end": v(74.25, -64.25) * mm});
            skLineSegment(sketch, "E79.18", {"start": v(-64.25, -74.25) * mm, "end": v(64.25, -74.25) * mm});
            skArc(sketch, "E79.19", {"start": v(-74.25, -64.25) * mm, "mid": v(-71.32, -71.32) * mm, "end": v(-64.25, -74.25) * mm});
            skLineSegment(sketch, "E80", {"start": v(-35.01, 74.25) * mm, "end": v(-17.01, 92.25) * mm});
            skLineSegment(sketch, "E81", {"start": v(-17.01, 92.25) * mm, "end": v(-17.01, 104.25) * mm});
            skLineSegment(sketch, "E82", {"start": v(30.99, 74.25) * mm, "end": v(12.99, 92.25) * mm});
            skLineSegment(sketch, "E83", {"start": v(12.99, 92.25) * mm, "end": v(12.99, 104.25) * mm});
            skArc(sketch, "E84", {"start": v(12.99, 104.25) * mm, "mid": v(-2.01, 119.25) * mm, "end": v(-17.01, 104.25) * mm});
            skPoint(sketch, "E85", {"position": v(0, 74.25) * mm});
            skLineSegment(sketch, "E86", {"start": v(30.99, -74.25) * mm, "end": v(12.99, -92.25) * mm});
            skLineSegment(sketch, "E87", {"start": v(12.99, -92.25) * mm, "end": v(12.99, -104.25) * mm});
            skLineSegment(sketch, "E88", {"start": v(-35.01, -74.25) * mm, "end": v(-17.01, -92.25) * mm});
            skLineSegment(sketch, "E89", {"start": v(-17.01, -92.25) * mm, "end": v(-17.01, -104.25) * mm});
            skArc(sketch, "E90", {"start": v(-17.01, -104.25) * mm, "mid": v(-2.01, -119.25) * mm, "end": v(12.99, -104.25) * mm});
            skCircle(sketch, "E91", {"center": v(-2.01, -104.25) * mm, "radius": 6 * mm});
            skCircle(sketch, "E92", {"center": v(-2.01, 104.25) * mm, "radius": 6 * mm});
            skSolve(sketch);
        }
        {
            var Q0;
            Q0 = qSketchRegion(id + "F16", true);
            extrude(context, id + "F17", {"entities" : qUnion([Q0]), "endBound" : BoundingType.SYMMETRIC, "depth" : 6 * mm});
        }
    });
